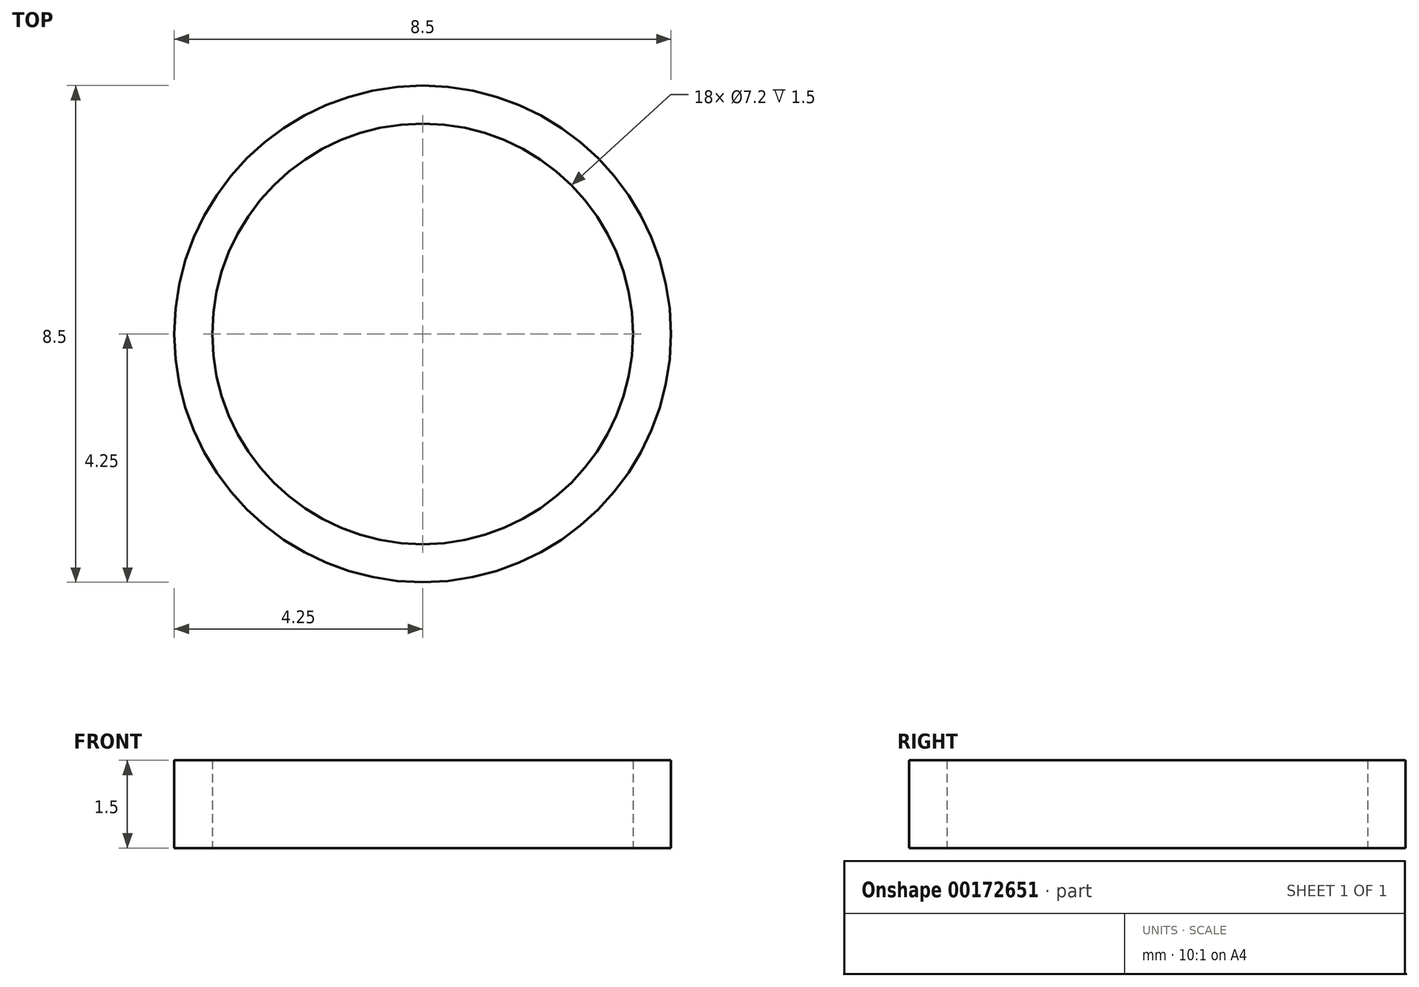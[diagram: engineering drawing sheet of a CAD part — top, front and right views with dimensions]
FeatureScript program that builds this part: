
annotation { "Feature Type Name" : "Feature", "Feature Type Description" : "" }
export const myFeature = defineFeature(function(context is Context, id is Id, definition is map)
    precondition{}
    {
        {
            var Q0;
            Q0=qCreatedBy(makeId("Top.planeOp"),FACE);
            var sketch = newSketch(context, id + "F0", { "sketchPlane" : qUnion([Q0])});
            skCircle(sketch, "E0", {"center": v(0, 0) * mm, "radius": 4.25 * mm});
            skCircle(sketch, "E1", {"center": v(0, 0) * mm, "radius": 3.6 * mm});
            skSolve(sketch);
        }
        {
            var Q0;
            Q0=makeQuery(id+"F0.imprint","IMPRINT",FACE,{"disambiguationData":[TD([[makeQuery(id+"F0.imprint","IMPRINT",EDGE,{"derivedFrom":sQuery(id+"F0.wireOp",EDGE,"E0")}),1.0]])]});
            extrude(context, id + "F1", {"entities" : qUnion([Q0]), "depth" : 1.5 * mm});
        }
    });
